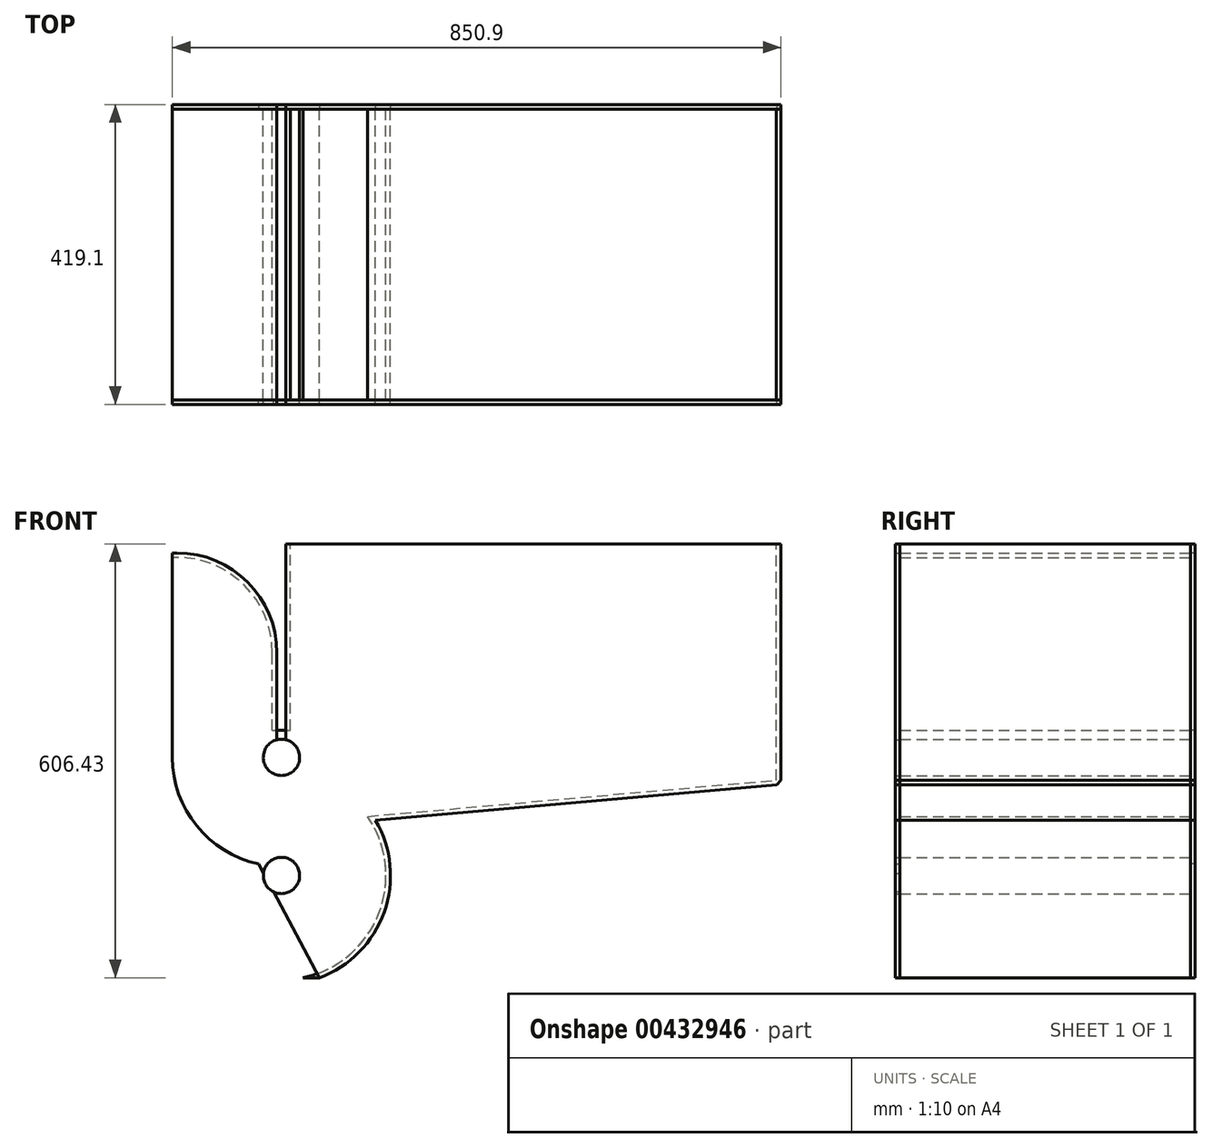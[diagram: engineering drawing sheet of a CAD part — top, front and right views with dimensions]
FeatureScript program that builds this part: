
annotation { "Feature Type Name" : "Feature", "Feature Type Description" : "" }
export const myFeature = defineFeature(function(context is Context, id is Id, definition is map)
    precondition{}
    {
        {
            var Q0;
            Q0=qCreatedBy(makeId("Front.planeOp"),FACE);
            var sketch = newSketch(context, id + "F0", { "sketchPlane" : qUnion([Q0])});
            skCircle(sketch, "E0", {"center": v(0, 146.05) * mm, "radius": 25.4 * mm});
            skArc(sketch, "E1", {"start": v(30.29, 3.18) * mm, "mid": v(135.6, 91.8) * mm, "end": v(120.48, 228.6) * mm});
            skCircle(sketch, "E2", {"center": v(0, 311.15) * mm, "radius": 25.4 * mm});
            skArc(sketch, "E3", {"start": v(-30.86, 168.4) * mm, "mid": v(-113.66, 219.43) * mm, "end": v(-146.05, 311.15) * mm});
            skLineSegment(sketch, "E4", {"start": v(-146.05, 311.15) * mm, "end": v(-146.05, 457.2) * mm});
            skLineSegment(sketch, "E5", {"start": v(-822.38, 0) * mm, "end": v(999.77, 0) * mm, "construction": true});
            skLineSegment(sketch, "E6.bottom", {"start": v(-234.95, 0) * mm, "end": v(781.05, 0) * mm, "construction": true});
            skLineSegment(sketch, "E6.top", {"start": v(-234.95, 609.6) * mm, "end": v(781.05, 609.6) * mm, "construction": true});
            skLineSegment(sketch, "E6.left", {"start": v(-234.95, 0) * mm, "end": v(-234.95, 609.6) * mm, "construction": true});
            skLineSegment(sketch, "E6.right", {"start": v(781.05, 0) * mm, "end": v(781.05, 609.6) * mm, "construction": true});
            skLineSegment(sketch, "E7", {"start": v(120.48, 228.6) * mm, "end": v(692.15, 279.4) * mm});
            skLineSegment(sketch, "E8", {"start": v(692.15, 279.4) * mm, "end": v(692.15, 609.6) * mm});
            skLineSegment(sketch, "E9", {"start": v(-107.9, 609.6) * mm, "end": v(692.15, 609.6) * mm});
            skArc(sketch, "E10.0", {"start": v(53.03, 3.18) * mm, "mid": v(143.56, 94.9) * mm, "end": v(131.43, 223.2) * mm});
            skLineSegment(sketch, "E11.0", {"start": v(131.43, 223.2) * mm, "end": v(692.71, 273.07) * mm});
            skLineSegment(sketch, "E12.0", {"start": v(698.5, 279.4) * mm, "end": v(698.5, 609.6) * mm});
            skArc(sketch, "E13.0", {"start": v(-32.2, 162.2) * mm, "mid": v(-118.6, 215.45) * mm, "end": v(-152.4, 311.15) * mm});
            skLineSegment(sketch, "E14.0", {"start": v(-152.4, 311.15) * mm, "end": v(-152.4, 457.2) * mm});
            skLineSegment(sketch, "E15", {"start": v(30.29, 3.18) * mm, "end": v(53.03, 3.18) * mm});
            skLineSegment(sketch, "E16", {"start": v(-32.2, 162.2) * mm, "end": v(-30.86, 168.4) * mm});
            skLineSegment(sketch, "E17", {"start": v(692.71, 273.07) * mm, "end": v(698.5, 279.4) * mm});
            skLineSegment(sketch, "E18", {"start": v(698.5, 609.6) * mm, "end": v(692.15, 609.6) * mm});
            skLineSegment(sketch, "E19.bottom", {"start": v(-12.7, 349.25) * mm, "end": v(-6.35, 349.25) * mm});
            skLineSegment(sketch, "E19.left", {"start": v(-12.7, 349.25) * mm, "end": v(-12.7, 457.2) * mm});
            skLineSegment(sketch, "E19.right", {"start": v(-6.35, 349.25) * mm, "end": v(-6.35, 457.2) * mm});
            skArc(sketch, "E20", {"start": v(-12.7, 457.2) * mm, "mid": v(-51.76, 551.5) * mm, "end": v(-146.05, 590.55) * mm});
            skArc(sketch, "E21", {"start": v(-6.35, 457.2) * mm, "mid": v(-47.27, 555.98) * mm, "end": v(-146.05, 596.9) * mm});
            skLineSegment(sketch, "E22.bottom", {"start": v(6.35, 349.25) * mm, "end": v(12.7, 349.25) * mm});
            skLineSegment(sketch, "E22.top", {"start": v(6.35, 609.6) * mm, "end": v(12.7, 609.6) * mm});
            skLineSegment(sketch, "E22.left", {"start": v(6.35, 349.25) * mm, "end": v(6.35, 609.6) * mm});
            skLineSegment(sketch, "E22.right", {"start": v(12.7, 349.25) * mm, "end": v(12.7, 609.6) * mm});
            skLineSegment(sketch, "E23", {"start": v(-152.4, 457.2) * mm, "end": v(-146.05, 457.2) * mm});
            skLineSegment(sketch, "E24.bottom", {"start": v(-146.05, 596.9) * mm, "end": v(-152.4, 596.9) * mm});
            skLineSegment(sketch, "E24.top", {"start": v(-146.05, 590.55) * mm, "end": v(-152.4, 590.55) * mm});
            skLineSegment(sketch, "E24.right", {"start": v(-152.4, 596.9) * mm, "end": v(-152.4, 590.55) * mm});
            skSolve(sketch);
        }
        {
            var Q0;
            Q0=makeQuery(id+"F0.imprint","IMPRINT",FACE,{"disambiguationData":[TD([[makeQuery(id+"F0.imprint","IMPRINT",EDGE,{"derivedFrom":sQuery(id+"F0.wireOp",EDGE,"E0")}),1.0]])]});
            var Q1;
            Q1=makeQuery(id+"F0.imprint","IMPRINT",FACE,{"disambiguationData":[TD([[makeQuery(id+"F0.imprint","IMPRINT",EDGE,{"derivedFrom":sQuery(id+"F0.wireOp",EDGE,"E3")}),1.0]])]});
            var Q2;
            Q2=makeQuery(id+"F0.imprint","IMPRINT",FACE,{"disambiguationData":[TD([[makeQuery(id+"F0.imprint","IMPRINT",EDGE,{"derivedFrom":sQuery(id+"F0.wireOp",EDGE,"E2")}),1.0]])]});
            var Q3;
            Q3=makeQuery(id+"F0.imprint","IMPRINT",FACE,{"disambiguationData":[TD([[makeQuery(id+"F0.imprint","IMPRINT",EDGE,{"derivedFrom":sQuery(id+"F0.wireOp",EDGE,"ENUjUcFZ-1Cq2-5GTR-Kzr8-PButdfUdz64S")}),1.0]])]});
            var Q4;
            Q4=makeQuery(id+"F0.imprint","IMPRINT",FACE,{"disambiguationData":[TD([[makeQuery(id+"F0.imprint","IMPRINT",EDGE,{"derivedFrom":sQuery(id+"F0.wireOp",EDGE,"E1")}),-1.0]])]});
            var Q5;
            Q5=makeQuery(id+"F0.imprint","IMPRINT",FACE,{"disambiguationData":[TD([[makeQuery(id+"F0.imprint","IMPRINT",EDGE,{"derivedFrom":sQuery(id+"F0.wireOp",EDGE,"HbfdHkyF-51qT-ZTV2-JNyR-PYeNqeTyp12F")}),1.0]])]});
            var Q6;
            Q6=makeQuery(id+"F0.imprint","IMPRINT",FACE,{"disambiguationData":[TD([[makeQuery(id+"F0.imprint","IMPRINT",EDGE,{"derivedFrom":sQuery(id+"F0.wireOp",EDGE,"E22.bottom")}),1.0]])]});
            var Q7;
            Q7=makeQuery(id+"F0.imprint","IMPRINT",FACE,{"disambiguationData":[TD([[makeQuery(id+"F0.imprint","IMPRINT",EDGE,{"derivedFrom":sQuery(id+"F0.wireOp",EDGE,"E19.bottom")}),1.0]])]});
            extrude(context, id + "F1", {"entities" : qUnion([Q0, Q1, Q2, Q3, Q4, Q5, Q6, Q7]), "depth" : 406.4 * mm});
        }
        {
            var Q0;
            Q0=qCreatedBy(makeId("Front.planeOp"),FACE);
            var sketch = newSketch(context, id + "F2", { "sketchPlane" : qUnion([Q0])});
            skLineSegment(sketch, "E25.0", {"start": v(698.5, 279.4) * mm, "end": v(698.5, 609.6) * mm});
            skLineSegment(sketch, "E26.0", {"start": v(131.43, 223.2) * mm, "end": v(692.71, 273.07) * mm});
            skArc(sketch, "E27.0", {"start": v(53.03, 3.18) * mm, "mid": v(143.56, 94.9) * mm, "end": v(131.43, 223.2) * mm});
            skArc(sketch, "E28.0", {"start": v(-32.2, 162.2) * mm, "mid": v(-118.6, 215.45) * mm, "end": v(-152.4, 311.15) * mm});
            skLineSegment(sketch, "E29.0", {"start": v(-152.4, 311.15) * mm, "end": v(-152.4, 457.2) * mm});
            skLineSegment(sketch, "E30", {"start": v(-32.2, 162.2) * mm, "end": v(53.03, 3.17) * mm});
            skLineSegment(sketch, "E31", {"start": v(692.15, 609.6) * mm, "end": v(698.5, 609.6) * mm});
            skLineSegment(sketch, "E32", {"start": v(692.71, 273.07) * mm, "end": v(698.5, 279.4) * mm});
            skLineSegment(sketch, "E33", {"start": v(698.5, 609.6) * mm, "end": v(6.35, 609.6) * mm});
            skLineSegment(sketch, "E34.0", {"start": v(6.35, 349.25) * mm, "end": v(6.35, 609.6) * mm});
            skArc(sketch, "E35.0", {"start": v(-6.35, 457.2) * mm, "mid": v(-47.27, 555.98) * mm, "end": v(-146.05, 596.9) * mm});
            skLineSegment(sketch, "E36.0", {"start": v(-6.35, 349.25) * mm, "end": v(-6.35, 457.2) * mm});
            skLineSegment(sketch, "E37", {"start": v(-6.35, 349.25) * mm, "end": v(6.35, 349.25) * mm});
            skLineSegment(sketch, "E38.0", {"start": v(-146.05, 596.9) * mm, "end": v(-152.4, 596.9) * mm});
            skLineSegment(sketch, "E39", {"start": v(-152.4, 596.9) * mm, "end": v(-152.4, 457.2) * mm});
            skSolve(sketch);
        }
        {
            var Q0;
            Q0=makeQuery(id+"F2.imprint","IMPRINT",FACE,{"disambiguationData":[TD([[makeQuery(id+"F2.imprint","IMPRINT",EDGE,{"derivedFrom":sQuery(id+"F2.wireOp",EDGE,"6a5e3f23-1e8a-4404-98ee-147f95c43414.0")}),-1.0]])]});
            var Q1;
            {var subQ2=sQuery(id+"F2.wireOp",EDGE,"E25.0");Q1=makeQuery(id+"F2.imprint","IMPRINT",FACE,{"disambiguationData":[TD([[makeQuery(id+"F2.imprint","IMPRINT",EDGE,{"derivedFrom":subQ2}),1.0]])]});}
            extrude(context, id + "F3", {"entities" : qUnion([Q0, Q1]), "oppositeDirection" : true, "depth" : 6.35 * mm});
        }
        {
            var Q0;
            Q0=makeQuery(id+"F1.opExtrude","CAP_FACE",FACE,{"disambiguationData":[OSD([sQuery(id+"F0.wireOp",EDGE,"E0")])],"isStart":false});
            var sketch = newSketch(context, id + "F4", { "sketchPlane" : qUnion([Q0])});
            skArc(sketch, "E40.0.0", {"start": v(-6.35, 457.2) * mm, "mid": v(-47.27, 555.98) * mm, "end": v(-146.05, 596.9) * mm});
            skLineSegment(sketch, "E40.0.1", {"start": v(-146.05, 596.9) * mm, "end": v(-152.4, 596.9) * mm});
            skLineSegment(sketch, "E40.0.2", {"start": v(-152.4, 596.9) * mm, "end": v(-152.4, 457.2) * mm});
            skLineSegment(sketch, "E40.0.3", {"start": v(-152.4, 457.2) * mm, "end": v(-152.4, 311.15) * mm});
            skArc(sketch, "E40.0.4", {"start": v(-152.4, 311.15) * mm, "mid": v(-118.6, 215.45) * mm, "end": v(-32.2, 162.2) * mm});
            skLineSegment(sketch, "E40.0.5", {"start": v(-32.2, 162.2) * mm, "end": v(53.03, 3.17) * mm});
            skArc(sketch, "E40.0.6", {"start": v(53.03, 3.18) * mm, "mid": v(143.56, 94.9) * mm, "end": v(131.43, 223.2) * mm});
            skLineSegment(sketch, "E40.0.7", {"start": v(131.43, 223.2) * mm, "end": v(692.71, 273.07) * mm});
            skLineSegment(sketch, "E40.0.8", {"start": v(692.71, 273.07) * mm, "end": v(698.5, 279.4) * mm});
            skLineSegment(sketch, "E40.0.9", {"start": v(698.5, 279.4) * mm, "end": v(698.5, 609.6) * mm});
            skLineSegment(sketch, "E40.0.10", {"start": v(698.5, 609.6) * mm, "end": v(6.35, 609.6) * mm});
            skLineSegment(sketch, "E40.0.11", {"start": v(6.35, 609.6) * mm, "end": v(6.35, 349.25) * mm});
            skLineSegment(sketch, "E40.0.13", {"start": v(-6.35, 349.25) * mm, "end": v(-6.35, 457.2) * mm});
            skArc(sketch, "E41.0", {"start": v(-6.35, 335.74) * mm, "mid": v(0, 285.75) * mm, "end": v(6.35, 335.74) * mm});
            skLineSegment(sketch, "E42", {"start": v(-6.35, 349.25) * mm, "end": v(-6.35, 335.74) * mm});
            skLineSegment(sketch, "E43", {"start": v(6.35, 349.25) * mm, "end": v(6.35, 335.74) * mm});
            skSolve(sketch);
        }
        {
            var Q0;
            {var subQ0=sQuery(id+"F4.wireOp",EDGE,"74d9abe5-d2a8-45a1-8a2a-545d3c43b958.0.0");Q0=makeQuery(id+"F4.imprint","IMPRINT",FACE,{"disambiguationData":[TD([[makeQuery(id+"F4.imprint","IMPRINT",EDGE,{"derivedFrom":subQ0}),1.0]])]});}
            var Q1;
            Q1=makeQuery(id+"F4.imprint","IMPRINT",FACE,{"disambiguationData":[TD([[makeQuery(id+"F4.imprint","IMPRINT",EDGE,{"derivedFrom":sQuery(id+"F4.wireOp",EDGE,"E40.0.0")}),1.0]])]});
            extrude(context, id + "F5", {"entities" : qUnion([Q0, Q1]), "depth" : 6.35 * mm});
        }
    });
